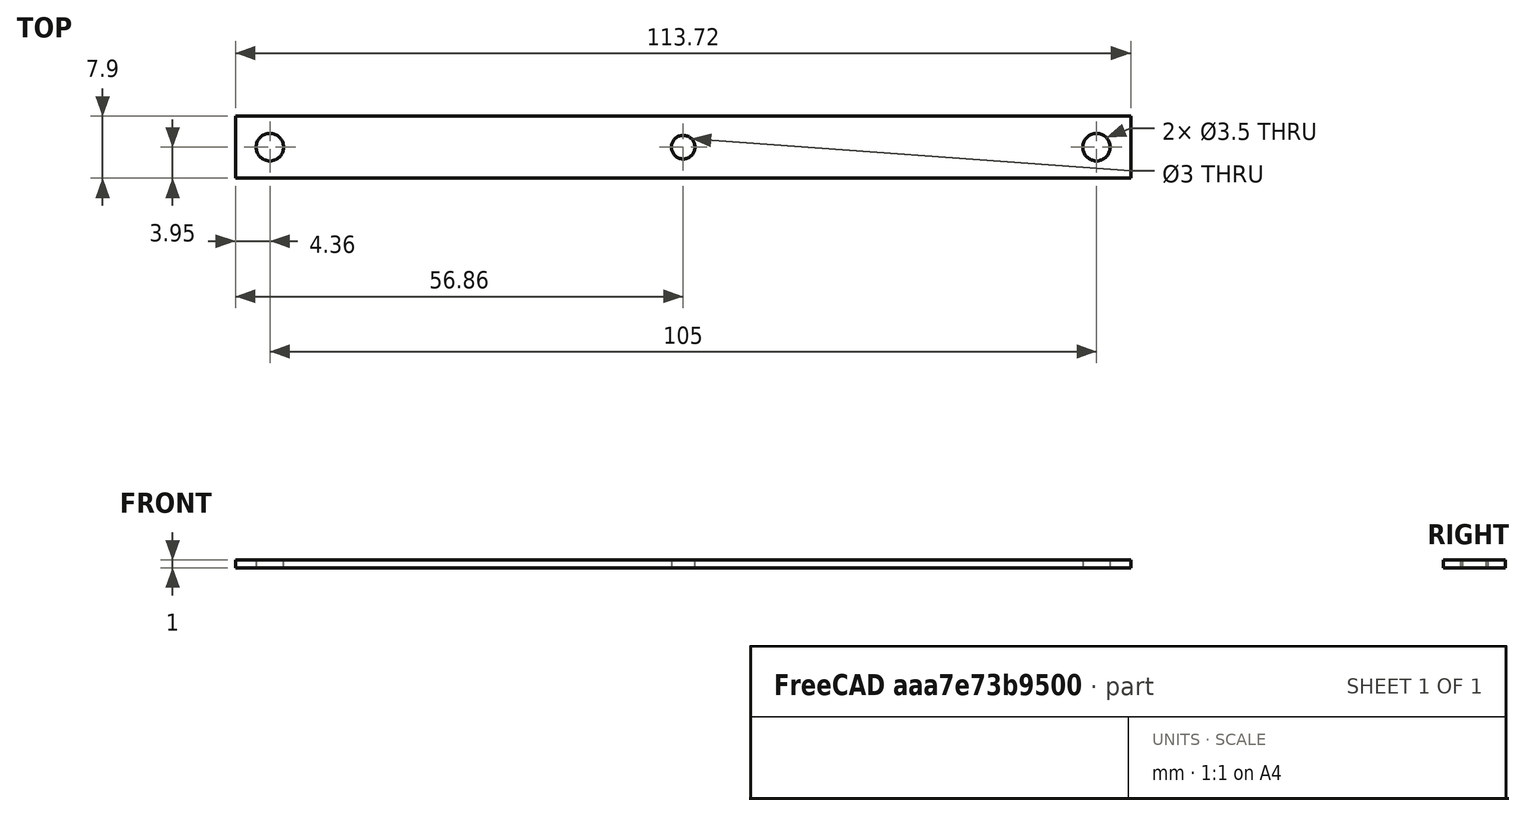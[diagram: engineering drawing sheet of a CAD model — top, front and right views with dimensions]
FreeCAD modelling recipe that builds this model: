
FCSTD DOCUMENT  (FreeCAD 2022.111R30764 (Git))
Label: bucket handle template
License: All rights reserved
LicenseURL: http://en.wikipedia.org/wiki/All_rights_reserved
objects: Sketcher::SketchObject×1, PartDesign::Pad×1, PartDesign::Body×1
note: 5 computed .brp shape members not serialized (recipe doc carries the construction recipe); baked Part::Feature solids carry a one-line shape summary decoded from their .brp

FEATURE [Sketcher::SketchObject] Sketch004
  FullyConstrained = false
  MapMode = 5
  Support = -> [XY_Plane]
  TreeRank = 16
  sketch-geometry (8):
    g0: Circle CenterX=-52.5 CenterY=0 CenterZ=0 NormalX=0 NormalY=0 NormalZ=1 AngleXU=0 Radius=1.75
    g1: Circle CenterX=52.5 CenterY=0 CenterZ=0 NormalX=0 NormalY=0 NormalZ=1 AngleXU=0 Radius=1.75
    g2: Circle CenterX=0 CenterY=0 CenterZ=0 NormalX=0 NormalY=0 NormalZ=1 AngleXU=0 Radius=1.5
    g3: LineSegment StartX=-56.8601 StartY=3.95192 StartZ=0 EndX=-56.8601 EndY=-3.95192 EndZ=0
    g4: LineSegment StartX=-56.8601 StartY=-3.95192 StartZ=0 EndX=56.8601 EndY=-3.95192 EndZ=0
    g5: LineSegment StartX=56.8601 StartY=-3.95192 StartZ=0 EndX=56.8601 EndY=3.95192 EndZ=0
    g6: LineSegment StartX=56.8601 StartY=3.95192 StartZ=0 EndX=-56.8601 EndY=3.95192 EndZ=0
    g7: GeomPoint [constr] X=0 Y=0 Z=0
  constraints (17):
    c: PointOnObject(g0,g-1)
    c: Equal(g1,g0)
    c: Symmetric(g1,g0,g-1)
    c: Diameter(g0) = 3.5
    c: DistanceX(g0,g1) = 105
    c: Coincident(g2,g-1)
    c: Diameter(g2) = 3
    c: Coincident(g3,g4)
    c: Coincident(g4,g5)
    c: Coincident(g5,g6)
    c: Coincident(g6,g3)
    c: Horizontal(g4)
    c: Horizontal(g6)
    c: Vertical(g3)
    c: Vertical(g5)
    c: Symmetric(g4,g3,g7)
    c: Coincident(g7,g2)
FEATURE [PartDesign::Pad] Pad
  AddSubType = 0
  AlongSketchNormal = false
  CheckUpToFaceLimits = true
  ClaimChildren = false
  Direction = (0,0,1)
  Fit = 0
  FitJoin = 0
  InnerFit = 0
  InnerFitJoin = 0
  InnerTaperAngle = 0
  InnerTaperAngleRev = 0
  Length = 1
  Length2 = 100
  Linearize = true
  NewSolid = false
  Profile = -> Sketch004
  Suppress = false
  TreeRank = 17
  Type = 0
  _ProfileBasedVersion = 1
FEATURE [PartDesign::Body] Body
  AutoGroupSolids = false
  ExportMode = 0
  Group = -> [Sketch004,Pad]
  Origin = -> Origin
  Tip = -> Pad
  TreeRank = 10
  _ExportChildren = -> [Pad]
  _GroupVersion = 1
